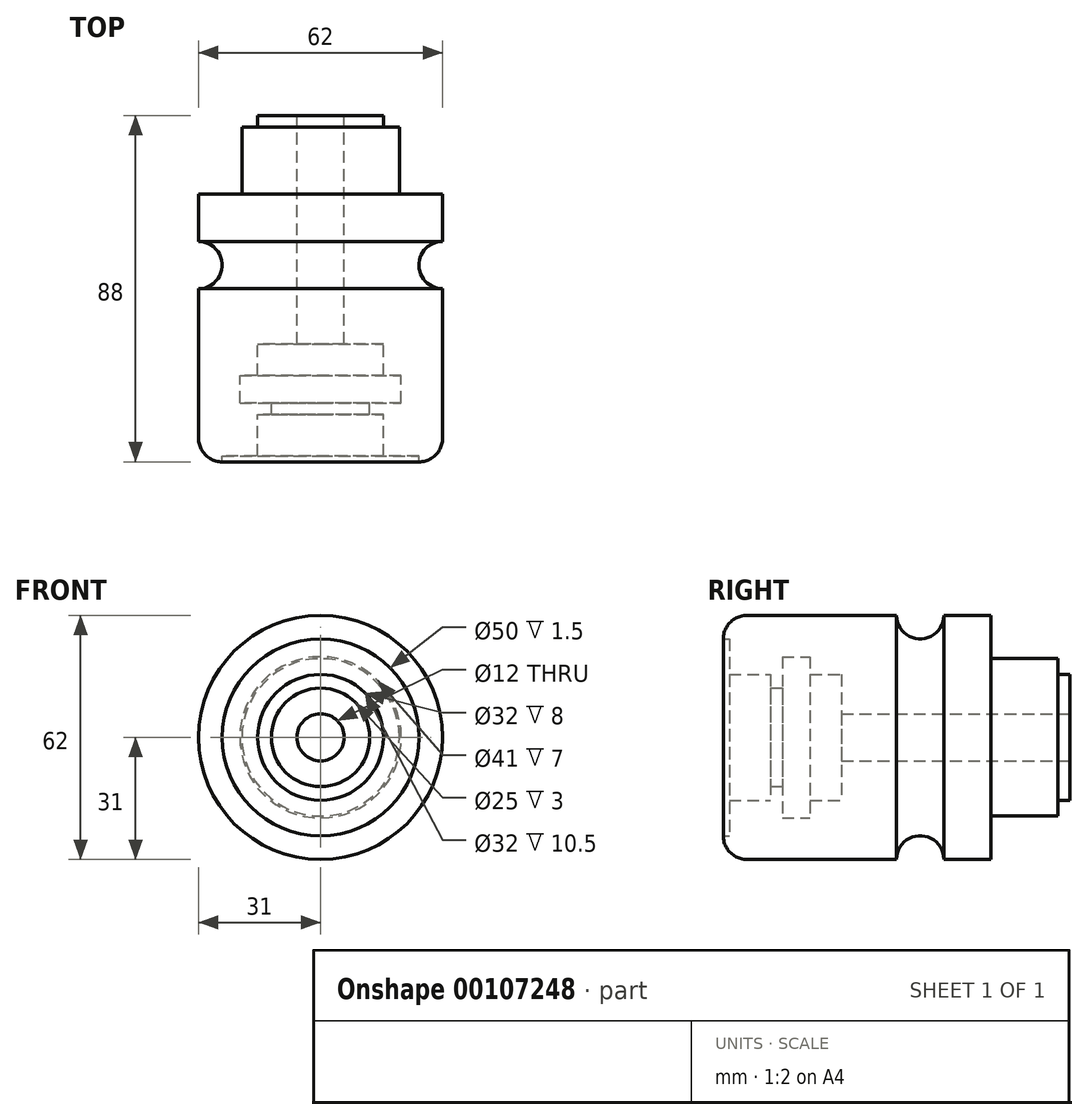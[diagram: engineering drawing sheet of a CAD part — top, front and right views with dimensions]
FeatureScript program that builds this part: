
annotation { "Feature Type Name" : "Feature", "Feature Type Description" : "" }
export const myFeature = defineFeature(function(context is Context, id is Id, definition is map)
    precondition{}
    {
        {
            var Q0;
            Q0=qCreatedBy(makeId("Right.planeOp"),FACE);
            var sketch = newSketch(context, id + "F0", { "sketchPlane" : qUnion([Q0])});
            skLineSegment(sketch, "E0", {"start": v(-59.46, 0) * mm, "end": v(68.6, 0) * mm, "construction": true});
            skLineSegment(sketch, "E1", {"start": v(-44, 31) * mm, "end": v(-44, 0) * mm});
            skLineSegment(sketch, "E2", {"start": v(-44, 31) * mm, "end": v(0, 31) * mm});
            skArc(sketch, "E3", {"start": v(0, 31) * mm, "mid": v(6, 25) * mm, "end": v(12, 31) * mm});
            skLineSegment(sketch, "E4", {"start": v(12, 31) * mm, "end": v(24, 31) * mm});
            skLineSegment(sketch, "E5", {"start": v(24, 31) * mm, "end": v(24, 0) * mm});
            skLineSegment(sketch, "E6", {"start": v(24, 0) * mm, "end": v(-44, 0) * mm});
            skSolve(sketch);
        }
        {
            var Q0;
            Q0 = qSketchRegion(id + "F0", true);
            var Q1;
            Q1=sQuery(id+"F0.wireOp",EDGE,"E0");
            revolve(context, id + "F1", {"entities" : qUnion([Q0]), "axis" : qUnion([Q1]), "revolveType" : RevolveType.FULL});
        }
        {
            var Q0;
            Q0=makeQuery(id+"F1.opRevolve","SWEPT_EDGE",EDGE,{"disambiguationData":[OSD([sQuery(id+"F0.wireOp",EDGE,"E1"),sQuery(id+"F0.wireOp",EDGE,"E2")])]});
            fillet(context, id + "F2", {"entities" : qUnion([Q0]), "radius" : 6 * mm, "tangentPropagation" : true, "allowEdgeOverflow" : false});
        }
        {
            var Q0;
            Q0=qCreatedBy(makeId("Right.planeOp"),FACE);
            var sketch = newSketch(context, id + "F3", { "sketchPlane" : qUnion([Q0])});
            skLineSegment(sketch, "E7", {"start": v(24, 20) * mm, "end": v(41, 20) * mm});
            skLineSegment(sketch, "E8", {"start": v(41, 20) * mm, "end": v(41, 16) * mm});
            skLineSegment(sketch, "E9", {"start": v(41, 16) * mm, "end": v(44, 16) * mm});
            skLineSegment(sketch, "E10", {"start": v(44, 16) * mm, "end": v(44, 0) * mm});
            skLineSegment(sketch, "E11", {"start": v(44, 0) * mm, "end": v(24, 0) * mm});
            skLineSegment(sketch, "E12", {"start": v(24, 0) * mm, "end": v(24, 20) * mm});
            skLineSegment(sketch, "E13", {"start": v(17.07, 0) * mm, "end": v(62.34, 0) * mm, "construction": true});
            skSolve(sketch);
        }
        {
            var Q0;
            Q0 = qSketchRegion(id + "F3", true);
            var Q1;
            Q1=sQuery(id+"F3.wireOp",EDGE,"E13");
            revolve(context, id + "F4", {"operationType" : NewBodyOperationType.ADD, "entities" : qUnion([Q0]), "axis" : qUnion([Q1]), "revolveType" : RevolveType.FULL});
        }
        {
            var Q0;
            Q0=qCreatedBy(makeId("Right.planeOp"),FACE);
            var sketch = newSketch(context, id + "F5", { "sketchPlane" : qUnion([Q0])});
            skLineSegment(sketch, "E14", {"start": v(-44, 25) * mm, "end": v(-42.5, 25) * mm});
            skLineSegment(sketch, "E15", {"start": v(-42.5, 25) * mm, "end": v(-42.5, 16) * mm});
            skLineSegment(sketch, "E16", {"start": v(-42.5, 16) * mm, "end": v(-32, 16) * mm});
            skLineSegment(sketch, "E17", {"start": v(-32, 16) * mm, "end": v(-32, 12.5) * mm});
            skLineSegment(sketch, "E18", {"start": v(-32, 12.5) * mm, "end": v(-29, 12.5) * mm});
            skLineSegment(sketch, "E19", {"start": v(-29, 12.5) * mm, "end": v(-29, 20.5) * mm});
            skLineSegment(sketch, "E20", {"start": v(-29, 20.5) * mm, "end": v(-22, 20.5) * mm});
            skLineSegment(sketch, "E21", {"start": v(-22, 20.5) * mm, "end": v(-22, 16) * mm});
            skLineSegment(sketch, "E22", {"start": v(-22, 16) * mm, "end": v(-14, 16) * mm});
            skLineSegment(sketch, "E23", {"start": v(-14, 16) * mm, "end": v(-14, 6) * mm});
            skLineSegment(sketch, "E24", {"start": v(-14, 6) * mm, "end": v(44, 6) * mm});
            skLineSegment(sketch, "E25", {"start": v(44, 6) * mm, "end": v(44, 0) * mm});
            skLineSegment(sketch, "E26", {"start": v(44, 0) * mm, "end": v(-44, 0) * mm});
            skLineSegment(sketch, "E27", {"start": v(-44, 0) * mm, "end": v(-44, 25) * mm});
            skLineSegment(sketch, "E28", {"start": v(-59.46, 0) * mm, "end": v(63.98, 0) * mm, "construction": true});
            skSolve(sketch);
        }
        {
            var Q0;
            Q0 = qSketchRegion(id + "F5", true);
            var Q1;
            Q1=sQuery(id+"F5.wireOp",EDGE,"E28");
            revolve(context, id + "F6", {"operationType" : NewBodyOperationType.REMOVE, "entities" : qUnion([Q0]), "axis" : qUnion([Q1]), "revolveType" : RevolveType.FULL, "oppositeDirection" : true});
        }
    });
